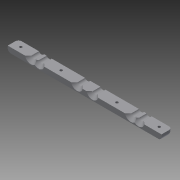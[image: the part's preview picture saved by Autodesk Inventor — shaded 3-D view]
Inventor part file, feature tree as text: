
AUTODESK INVENTOR PART (.ipt)
format: ipt  version: 2014 (Build 180170000, 170)  size: 242,688 bytes
history: native  units: mm
features: extrude x4, sketch x4, chamfer x2, fillet x1
ambient origin geometry x8: Origin, YZ Plane, XZ Plane, XY Plane, X Axis, Y Axis, Z Axis, Center Point
bodies: Solid1 (feature_tree)
feature tree (11):
  extrude  "Extrusion1"  Depth=7.0mm
  extrude  "Extrusion2"  Depth=14.0mm
  extrude  "Extrusion3"  Depth=30.0mm
  extrude  "Extrusion4"  Depth=4.0mm
  chamfer  "Chamfer1"  Distance=8.75mm
  chamfer  "Chamfer2"  Distance=7.5mm
  fillet  "Fillet1"  Radius=7.5mm
  sketch  "Sketch1"  dims[d0=200.0mm d1=7.0mm]
  sketch  "Sketch2"  dims[d2=14.0mm d3=0.0mm d4=7.5mm]
  sketch  "Sketch4"  dims[d5=7.5mm d6=30.0mm]
  sketch  "Sketch5"  dims[d7=40.0mm d8=8.75mm d9=8.75mm d10=7.5mm d11=7.5mm d12=7.5mm d13=7.5mm d14=90.0mm d15=110.0mm d16=160.0mm d17=170.0mm d18=14.0mm d19=0.0mm d20=8.75mm d21=8.75mm d22=8.75mm d23=8.75mm d24=3.4mm d25=3.4mm d26=3.4mm d27=3.4mm d28=10.0mm d29=65.0mm d30=137.5mm d31=10.0mm d32=14.0mm d33=0.0mm d34=6.4mm d35=6.4mm d36=6.4mm d37=6.4mm d38=2.4mm d39=0.0mm d40=0.5mm d41=2.0mm d42=45.0deg d43=4.0mm d44=2.0mm d45=45.0deg d46=4.0mm]
